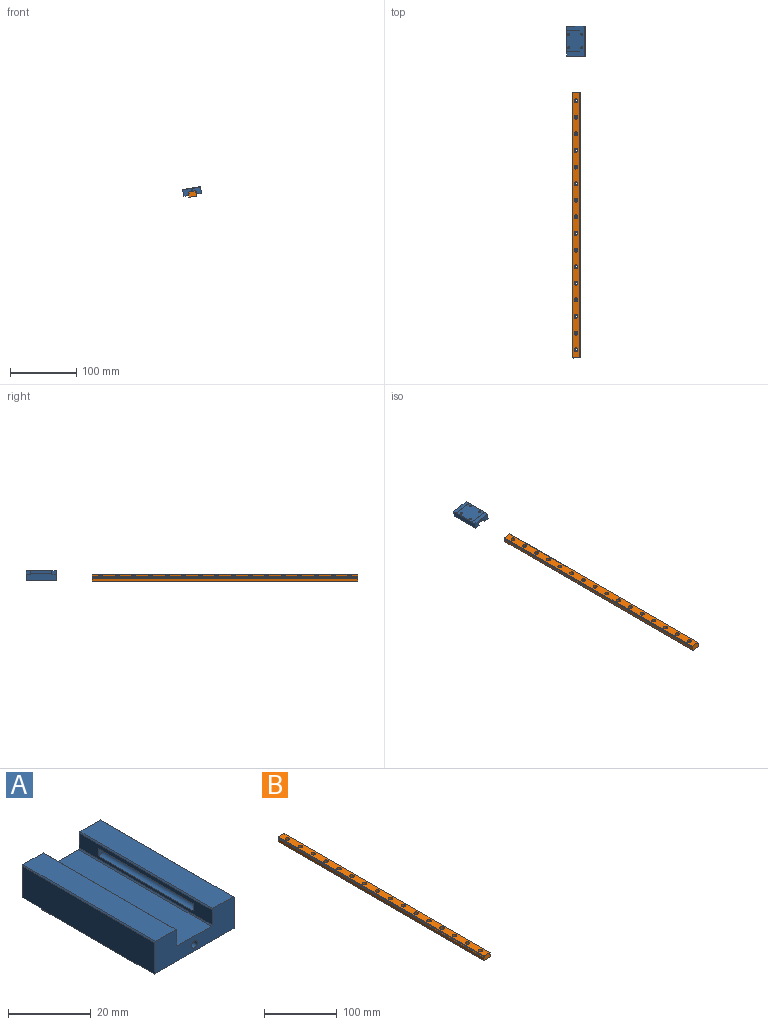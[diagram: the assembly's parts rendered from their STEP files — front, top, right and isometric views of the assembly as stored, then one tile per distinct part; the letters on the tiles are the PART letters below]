
ASSEMBLY  parts=2 mates=1
PART A: 37 faces, bbox 27x45.4x10 mm
  f0: plane 45.4x0.3mm, normal (-0.71,0,0.71), area 19.3mm2, adj f3,f6,f22,f23
  f1: plane 45.4x0.3mm, normal (0.71,0,0.71), area 19.3mm2, adj f10,f11,f22,f23
  f2: plane 45.4x0.3mm, normal (0.71,0,0.71), area 19.3mm2, adj f6,f7,f22,f23
  f3: plane 45.4x4.4mm, normal (-1,0,0), area 129.2mm2, adj f0,f5,f17,f20,f22,f23,f24
  f4: plane 45.4x11.4mm, normal (0,0,1), area 517.6mm2, adj f16,f17,f22,f23
  f5: cylinder r=1.15mm len=32.4mm, axis (0,-1,0), area 141.5mm2, adj f3,f20,f24
  f6: plane 45.4x6.9mm, normal (0,0,1), area 313.3mm2, adj f0,f2,f22,f23
  f7: plane 45.4x9.4mm, normal (1,0,0), area 424.2mm2, adj f2,f15,f18,f21,f22,f23,f25,f35
  f8: plane 32.4x26.4mm, normal (0,0,-1), area 821.1mm2, adj f14,f15,f18,f27,f29,f31,f33,f35
  f9: plane 45.4x9.4mm, normal (-1,0,0), area 424.2mm2, adj f14,f18,f21,f22,f23,f25,f34,f35
  f10: plane 45.4x6.9mm, normal (0,0,1), area 313.3mm2, adj f1,f22,f23,f34
  f11: plane 45.4x4.4mm, normal (1,0,0), area 129.2mm2, adj f1,f12,f16,f19,f22,f23,f36
  f12: cylinder r=1.15mm len=32.4mm, axis (0,-1,0), area 141.5mm2, adj f11,f19,f36
  f13: cylinder r=1mm len=45.4mm, axis (0,-1,0), area 285.3mm2, adj f22,f23
  f14: plane 32.4x0.3mm, normal (-0.71,0,-0.71), area 13.7mm2, adj f8,f9,f18,f35
  f15: plane 32.4x0.3mm, normal (0.71,0,-0.71), area 13.7mm2, adj f7,f8,f18,f35
  f16: plane 45.4x0.3mm, normal (0.71,0,0.71), area 19.3mm2, adj f4,f11,f22,f23
  f17: plane 45.4x0.3mm, normal (-0.71,0,0.71), area 19.3mm2, adj f3,f4,f22,f23
  f18: plane 27x0.5mm, normal (0,-1,0), area 13.4mm2, adj f7,f8,f9,f14,f15,f21
  f19: plane 2.3x1.52mm, normal (0,1,0), area 2.9mm2, adj f11,f12
  f20: plane 2.3x1.52mm, normal (0,1,0), area 2.9mm2, adj f3,f5
  f21: plane 27x6.5mm, normal (0,0,-1), area 175.5mm2, adj f7,f9,f18,f22
  f22: plane 27x9.5mm, normal (0,-1,0), area 193.3mm2, adj f0,f1,f2,f3,f4,f6,f7,f9
  f23: plane 27x9.5mm, normal (0,1,0), area 193.3mm2, adj f0,f1,f2,f3,f4,f6,f7,f9
  f24: plane 2.3x1.52mm, normal (0,-1,0), area 2.9mm2, adj f3,f5
  f25: plane 27x6.5mm, normal (0,0,-1), area 175.5mm2, adj f7,f9,f23,f35
  f26: cone r=857.17mm half-angle=59deg, axis (0,0,-1), area 10mm2, adj f27
  f27: cylinder r=1.65mm len=3.5mm, axis (0,0,1), area 36.3mm2, adj f8,f26
  f28: cone r=857.17mm half-angle=59deg, axis (0,0,-1), area 10mm2, adj f29
  f29: cylinder r=1.65mm len=3.5mm, axis (0,0,1), area 36.3mm2, adj f8,f28
  f30: cone r=857.17mm half-angle=59deg, axis (0,0,-1), area 10mm2, adj f31
  f31: cylinder r=1.65mm len=3.5mm, axis (0,0,1), area 36.3mm2, adj f8,f30
  f32: cone r=857.17mm half-angle=59deg, axis (0,0,-1), area 10mm2, adj f33
  f33: cylinder r=1.65mm len=3.5mm, axis (0,0,1), area 36.3mm2, adj f8,f32
  f34: plane 45.4x0.3mm, normal (-0.71,0,0.71), area 19.3mm2, adj f9,f10,f22,f23
  f35: plane 27x0.5mm, normal (0,1,0), area 13.4mm2, adj f7,f8,f9,f14,f15,f25
  f36: plane 2.3x1.52mm, normal (0,-1,0), area 2.9mm2, adj f11,f12
PART B: 70 faces, bbox 12x400x8 mm
  f0: plane 400x0.51mm, normal (0,0,1), area 203.9mm2, adj f1,f19,f20,f51
  f1: plane 400x0.3mm, normal (1,0,0), area 120mm2, adj f0,f2,f20,f51
  f2: plane 400x0.51mm, normal (0,0,-1), area 203.9mm2, adj f1,f3,f20,f51
  f3: cylinder r=1.15mm len=400mm, axis (0,1,0), area 511.7mm2, adj f2,f4,f20,f51
  f4: plane 400x0.86mm, normal (1,0,0), area 344.4mm2, adj f3,f5,f20,f51
  f5: plane 400x0.35mm, normal (0.71,0,0.71), area 198mm2, adj f4,f6,f20,f51
  f6: plane 400x11.3mm, normal (0,0,1), area 4067.6mm2, adj f5,f7,f20,f23,f26,f29,f32,f35
  f7: plane 400x0.35mm, normal (-0.71,0,0.71), area 198mm2, adj f6,f8,f20,f51
  f8: plane 400x0.86mm, normal (-1,0,0), area 344.4mm2, adj f7,f9,f20,f51
  f9: cylinder r=1.15mm len=400mm, axis (0,1,0), area 511.7mm2, adj f8,f10,f20,f51
  f10: plane 400x0.51mm, normal (0,0,-1), area 203.9mm2, adj f9,f11,f20,f51
  f11: plane 400x0.3mm, normal (-1,0,0), area 120mm2, adj f10,f12,f20,f51
  f12: plane 400x0.51mm, normal (0,0,1), area 203.9mm2, adj f11,f13,f20,f51
  f13: cylinder r=1.15mm len=400mm, axis (0,1,0), area 511.7mm2, adj f12,f14,f20,f51
  f14: plane 400x4.26mm, normal (-1,0,0), area 1704.5mm2, adj f13,f15,f20,f51
  f15: plane 400x0.35mm, normal (-0.71,0,-0.71), area 198mm2, adj f14,f16,f20,f51
  f16: plane 400x11.3mm, normal (0,0,-1), area 4366.1mm2, adj f15,f17,f20,f21,f24,f27,f30,f33
  f17: plane 400x0.35mm, normal (0.71,0,-0.71), area 198mm2, adj f16,f18,f20,f51
  f18: plane 400x4.26mm, normal (1,0,0), area 1704.5mm2, adj f17,f19,f20,f51
  f19: cylinder r=1.15mm len=400mm, axis (0,1,0), area 511.7mm2, adj f0,f18,f20,f51
  f20: plane 12x8mm, normal (0,-1,0), area 93mm2, adj f0,f1,f2,f3,f4,f5,f6,f7
  f21: cylinder r=1.75mm len=3.5mm, axis (0,0,1), area 38.5mm2, adj f16,f22
  f22: plane 6x6mm, normal (0,0,1), area 18.7mm2, adj f21,f23
  f23: cylinder r=3mm len=6mm, axis (0,0,1), area 84.8mm2, adj f6,f22
  f24: cylinder r=1.75mm len=3.5mm, axis (0,0,1), area 38.5mm2, adj f16,f25
  f25: plane 6x6mm, normal (0,0,1), area 18.7mm2, adj f24,f26
  f26: cylinder r=3mm len=6mm, axis (0,0,1), area 84.8mm2, adj f6,f25
  f27: cylinder r=1.75mm len=3.5mm, axis (0,0,1), area 38.5mm2, adj f16,f28
  f28: plane 6x6mm, normal (0,0,1), area 18.7mm2, adj f27,f29
  f29: cylinder r=3mm len=6mm, axis (0,0,1), area 84.8mm2, adj f6,f28
  f30: cylinder r=1.75mm len=3.5mm, axis (0,0,1), area 38.5mm2, adj f16,f31
  f31: plane 6x6mm, normal (0,0,1), area 18.7mm2, adj f30,f32
  f32: cylinder r=3mm len=6mm, axis (0,0,1), area 84.8mm2, adj f6,f31
  f33: cylinder r=1.75mm len=3.5mm, axis (0,0,1), area 38.5mm2, adj f16,f34
  f34: plane 6x6mm, normal (0,0,1), area 18.7mm2, adj f33,f35
  f35: cylinder r=3mm len=6mm, axis (0,0,1), area 84.8mm2, adj f6,f34
  f36: cylinder r=1.75mm len=3.5mm, axis (0,0,1), area 38.5mm2, adj f16,f37
  f37: plane 6x6mm, normal (0,0,1), area 18.7mm2, adj f36,f38
  f38: cylinder r=3mm len=6mm, axis (0,0,1), area 84.8mm2, adj f6,f37
  f39: cylinder r=1.75mm len=3.5mm, axis (0,0,1), area 38.5mm2, adj f16,f40
  f40: plane 6x6mm, normal (0,0,1), area 18.7mm2, adj f39,f41
  f41: cylinder r=3mm len=6mm, axis (0,0,1), area 84.8mm2, adj f6,f40
  f42: cylinder r=1.75mm len=3.5mm, axis (0,0,1), area 38.5mm2, adj f16,f43
  f43: plane 6x6mm, normal (0,0,1), area 18.7mm2, adj f42,f44
  f44: cylinder r=3mm len=6mm, axis (0,0,1), area 84.8mm2, adj f6,f43
  f45: cylinder r=1.75mm len=3.5mm, axis (0,0,1), area 38.5mm2, adj f16,f46
  f46: plane 6x6mm, normal (0,0,1), area 18.7mm2, adj f45,f47
  f47: cylinder r=3mm len=6mm, axis (0,0,1), area 84.8mm2, adj f6,f46
  f48: cylinder r=1.75mm len=3.5mm, axis (0,0,1), area 38.5mm2, adj f16,f49
  f49: plane 6x6mm, normal (0,0,1), area 18.7mm2, adj f48,f50
  f50: cylinder r=3mm len=6mm, axis (0,0,1), area 84.8mm2, adj f6,f49
  f51: plane 12x8mm, normal (0,1,0), area 93mm2, adj f0,f1,f2,f3,f4,f5,f6,f7
  f52: cylinder r=1.75mm len=3.5mm, axis (0,0,1), area 38.5mm2, adj f16,f53
  f53: plane 6x6mm, normal (0,0,1), area 18.7mm2, adj f52,f54
  f54: cylinder r=3mm len=6mm, axis (0,0,1), area 84.8mm2, adj f6,f53
  f55: cylinder r=1.75mm len=3.5mm, axis (0,0,1), area 38.5mm2, adj f16,f56
  f56: plane 6x6mm, normal (0,0,1), area 18.7mm2, adj f55,f57
  f57: cylinder r=3mm len=6mm, axis (0,0,1), area 84.8mm2, adj f6,f56
  f58: cylinder r=1.75mm len=3.5mm, axis (0,0,1), area 38.5mm2, adj f16,f59
  f59: plane 6x6mm, normal (0,0,1), area 18.7mm2, adj f58,f60
  f60: cylinder r=3mm len=6mm, axis (0,0,1), area 84.8mm2, adj f6,f59
  f61: cylinder r=1.75mm len=3.5mm, axis (0,0,1), area 38.5mm2, adj f16,f62
  f62: plane 6x6mm, normal (0,0,1), area 18.7mm2, adj f61,f63
  f63: cylinder r=3mm len=6mm, axis (0,0,1), area 84.8mm2, adj f6,f62
  f64: cylinder r=1.75mm len=3.5mm, axis (0,0,1), area 38.5mm2, adj f16,f65
  f65: plane 6x6mm, normal (0,0,1), area 18.7mm2, adj f64,f66
  f66: cylinder r=3mm len=6mm, axis (0,0,1), area 84.8mm2, adj f6,f65
  f67: cylinder r=1.75mm len=3.5mm, axis (0,0,1), area 38.5mm2, adj f16,f68
  f68: plane 6x6mm, normal (0,0,1), area 18.7mm2, adj f67,f69
  f69: cylinder r=3mm len=6mm, axis (0,0,1), area 84.8mm2, adj f6,f68
PLACE A rot(axis=(0,1,0),170deg) t=(60.48,155.99,103.06)mm
PLACE B rot(axis=(0,-1,0),10deg) t=(60.48,-312.36,103.06)mm
MATE slider B.f20 <-> A.f22  axis (0,-1,0) through (60.48,-337.36,103.06)mm
